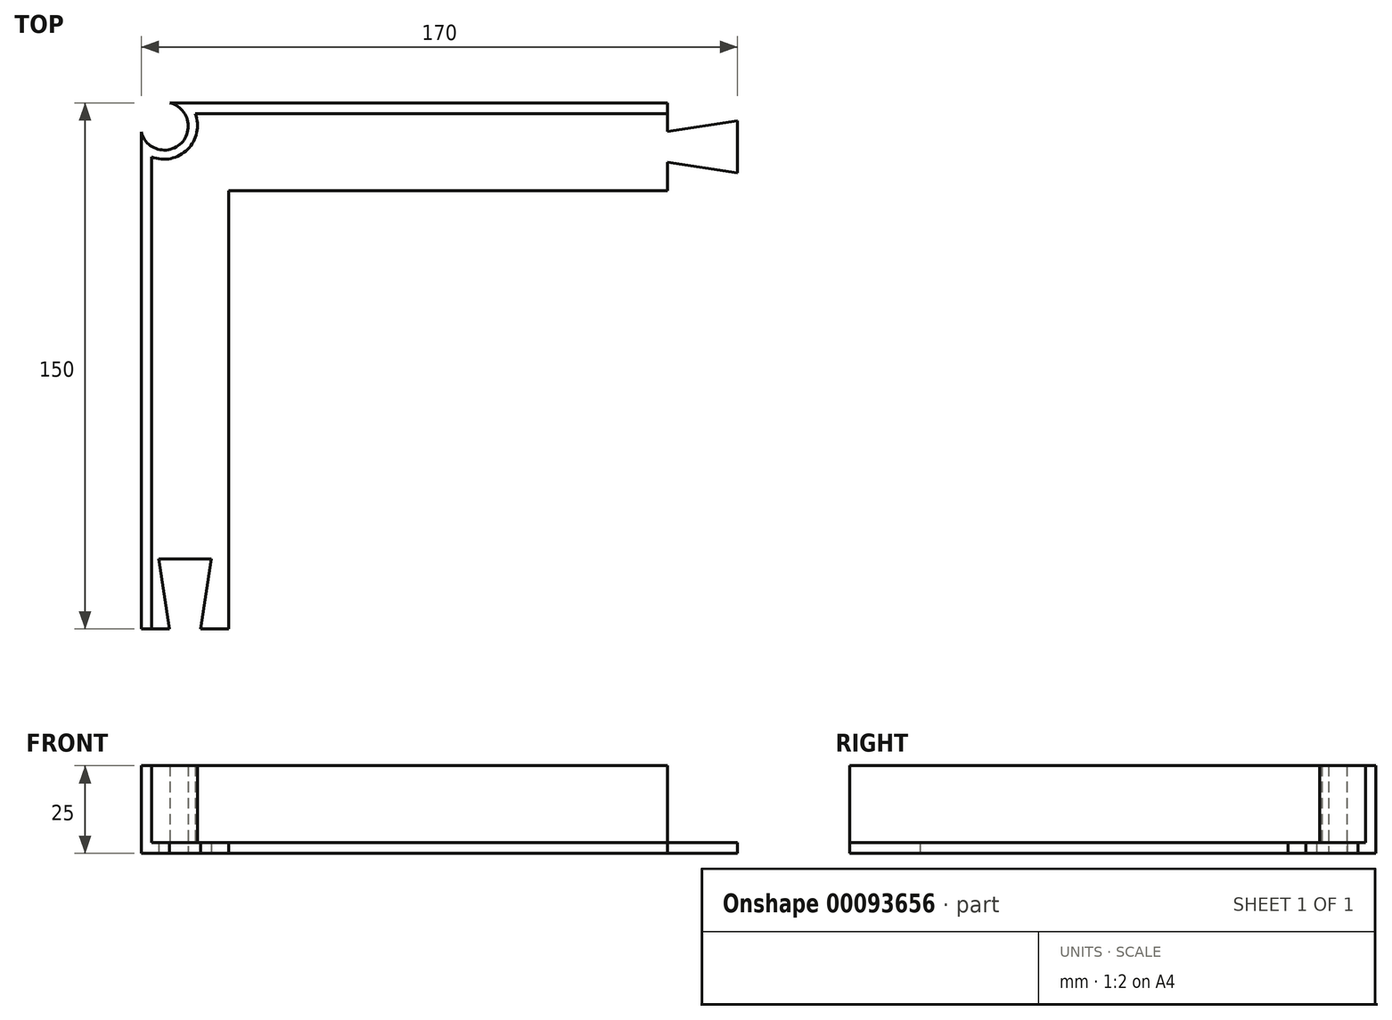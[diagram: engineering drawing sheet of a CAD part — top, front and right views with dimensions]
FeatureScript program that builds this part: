
annotation { "Feature Type Name" : "Feature", "Feature Type Description" : "" }
export const myFeature = defineFeature(function(context is Context, id is Id, definition is map)
    precondition{}
    {
        {
            var Q0;
            Q0=qCreatedBy(makeId("Top.planeOp"),FACE);
            var sketch = newSketch(context, id + "F0", { "sketchPlane" : qUnion([Q0])});
            skLineSegment(sketch, "E0.bottom", {"start": v(-150, 150) * mm, "end": v(150, 150) * mm});
            skLineSegment(sketch, "E0.top", {"start": v(-150, -150) * mm, "end": v(150, -150) * mm});
            skLineSegment(sketch, "E0.left", {"start": v(-150, 150) * mm, "end": v(-150, -150) * mm});
            skLineSegment(sketch, "E0.right", {"start": v(150, 150) * mm, "end": v(150, -150) * mm});
            skPoint(sketch, "E0.middle", {"position": v(0, 0) * mm});
            skLineSegment(sketch, "E1.bottom", {"start": v(-125, 125) * mm, "end": v(125, 125) * mm});
            skLineSegment(sketch, "E1.top", {"start": v(-125, -125) * mm, "end": v(125, -125) * mm});
            skLineSegment(sketch, "E1.left", {"start": v(-125, 125) * mm, "end": v(-125, -125) * mm});
            skLineSegment(sketch, "E1.right", {"start": v(125, 125) * mm, "end": v(125, -125) * mm});
            skArc(sketch, "E2", {"start": v(-150, 145) * mm, "mid": v(-138.57, 138.57) * mm, "end": v(-145, 150) * mm});
            skArc(sketch, "E3", {"start": v(138, 150) * mm, "mid": v(138.34, 138.34) * mm, "end": v(150, 138) * mm});
            skArc(sketch, "E4", {"start": v(150, -138) * mm, "mid": v(138.34, -138.34) * mm, "end": v(138, -150) * mm});
            skArc(sketch, "E5", {"start": v(-138, -150) * mm, "mid": v(-138.34, -138.34) * mm, "end": v(-150, -138) * mm});
            skLineSegment(sketch, "E6", {"start": v(-213.2, 0) * mm, "end": v(261.8, 0) * mm, "construction": true});
            skLineSegment(sketch, "E7", {"start": v(0, 181.59) * mm, "end": v(0, -172.22) * mm, "construction": true});
            skPoint(sketch, "E7.endSnap0", {"position": v(0, -150) * mm});
            skLineSegment(sketch, "E8", {"start": v(-213.2, 20) * mm, "end": v(261.8, 20) * mm, "construction": true});
            skLineSegment(sketch, "E9.MirrorCS", {"start": v(-213.2, -20) * mm, "end": v(261.8, -20) * mm, "construction": true});
            skLineSegment(sketch, "E10", {"start": v(20, -172.22) * mm, "end": v(20, 181.59) * mm, "construction": true});
            skLineSegment(sketch, "E11.MirrorCS", {"start": v(-20, -172.22) * mm, "end": v(-20, 181.59) * mm, "construction": true});
            skLineSegment(sketch, "E12", {"start": v(-150, 0) * mm, "end": v(-142, 0) * mm});
            skLineSegment(sketch, "E13", {"start": v(-142, 0) * mm, "end": v(-145, 20) * mm});
            skLineSegment(sketch, "E14", {"start": v(-145, 20) * mm, "end": v(-130, 20) * mm});
            skLineSegment(sketch, "E15", {"start": v(-130, 20) * mm, "end": v(-133, 0) * mm});
            skLineSegment(sketch, "E16", {"start": v(-133, 0) * mm, "end": v(-125, 0) * mm});
            skLineSegment(sketch, "E17", {"start": v(125, 0) * mm, "end": v(133, 0) * mm});
            skLineSegment(sketch, "E18", {"start": v(133, 0) * mm, "end": v(130, -20) * mm});
            skLineSegment(sketch, "E19", {"start": v(130, -20) * mm, "end": v(145, -20) * mm});
            skLineSegment(sketch, "E20", {"start": v(145, -20) * mm, "end": v(142, 0) * mm});
            skLineSegment(sketch, "E21", {"start": v(142, 0) * mm, "end": v(150, 0) * mm});
            skLineSegment(sketch, "E22", {"start": v(0, -150) * mm, "end": v(0, -142) * mm});
            skLineSegment(sketch, "E23", {"start": v(0, -142) * mm, "end": v(-20, -145) * mm});
            skLineSegment(sketch, "E24", {"start": v(-20, -145) * mm, "end": v(-20, -130) * mm});
            skLineSegment(sketch, "E25", {"start": v(-20, -130) * mm, "end": v(0, -133) * mm});
            skLineSegment(sketch, "E26", {"start": v(0, -133) * mm, "end": v(0, -125) * mm});
            skLineSegment(sketch, "E27", {"start": v(0, 150) * mm, "end": v(0, 141.9) * mm});
            skLineSegment(sketch, "E28", {"start": v(0, 141.9) * mm, "end": v(20, 144.9) * mm});
            skLineSegment(sketch, "E29", {"start": v(20, 144.9) * mm, "end": v(20, 130.1) * mm});
            skLineSegment(sketch, "E30", {"start": v(20, 130.1) * mm, "end": v(0, 133.1) * mm});
            skLineSegment(sketch, "E31", {"start": v(0, 133.1) * mm, "end": v(0, 125) * mm});
            skLineSegment(sketch, "E32", {"start": v(-137.61, 147) * mm, "end": v(0, 147) * mm});
            skPoint(sketch, "E32.endSnap0", {"position": v(0, 145.95) * mm});
            skLineSegment(sketch, "E33", {"start": v(-147, 137.61) * mm, "end": v(-147, 0) * mm});
            skArc(sketch, "E34", {"start": v(-147, 134.61) * mm, "mid": v(-136.77, 136.77) * mm, "end": v(-134.61, 147) * mm});
            skSolve(sketch);
        }
        {
            var Q0;
            {var subQ3=sQuery(id+"F0.wireOp",EDGE,"E13");Q0=makeQuery(id+"F0.imprint","IMPRINT",FACE,{"disambiguationData":[TD([[makeQuery(id+"F0.imprint","IMPRINT",EDGE,{"derivedFrom":subQ3}),1.0]])]});}
            extrude(context, id + "F1", {"entities" : qUnion([Q0]), "depth" : 3 * mm});
        }
        {
            var Q0;
            {var subQ5=sQuery(id+"F0.wireOp",EDGE,"E33");Q0=makeQuery(id+"F0.imprint","IMPRINT",FACE,{"disambiguationData":[TD([[makeQuery(id+"F0.imprint","IMPRINT",EDGE,{"derivedFrom":subQ5}),-1.0]])]});}
            var Q1;
            {var subQ5=sQuery(id+"F0.wireOp",EDGE,"E32");Q1=makeQuery(id+"F0.imprint","IMPRINT",FACE,{"disambiguationData":[TD([[makeQuery(id+"F0.imprint","IMPRINT",EDGE,{"derivedFrom":subQ5}),1.0]])]});}
            extrude(context, id + "F2", {"entities" : qUnion([Q0, Q1]), "operationType" : NewBodyOperationType.ADD, "depth" : 25 * mm});
        }
        {
            var Q0;
            {var subQ5=sQuery(id+"F0.wireOp",EDGE,"E34");Q0=makeQuery(id+"F0.imprint","IMPRINT",FACE,{"disambiguationData":[TD([[makeQuery(id+"F0.imprint","IMPRINT",EDGE,{"derivedFrom":subQ5}),1.0]])]});}
            extrude(context, id + "F3", {"entities" : qUnion([Q0]), "operationType" : NewBodyOperationType.ADD, "depth" : 25 * mm});
        }
    });
